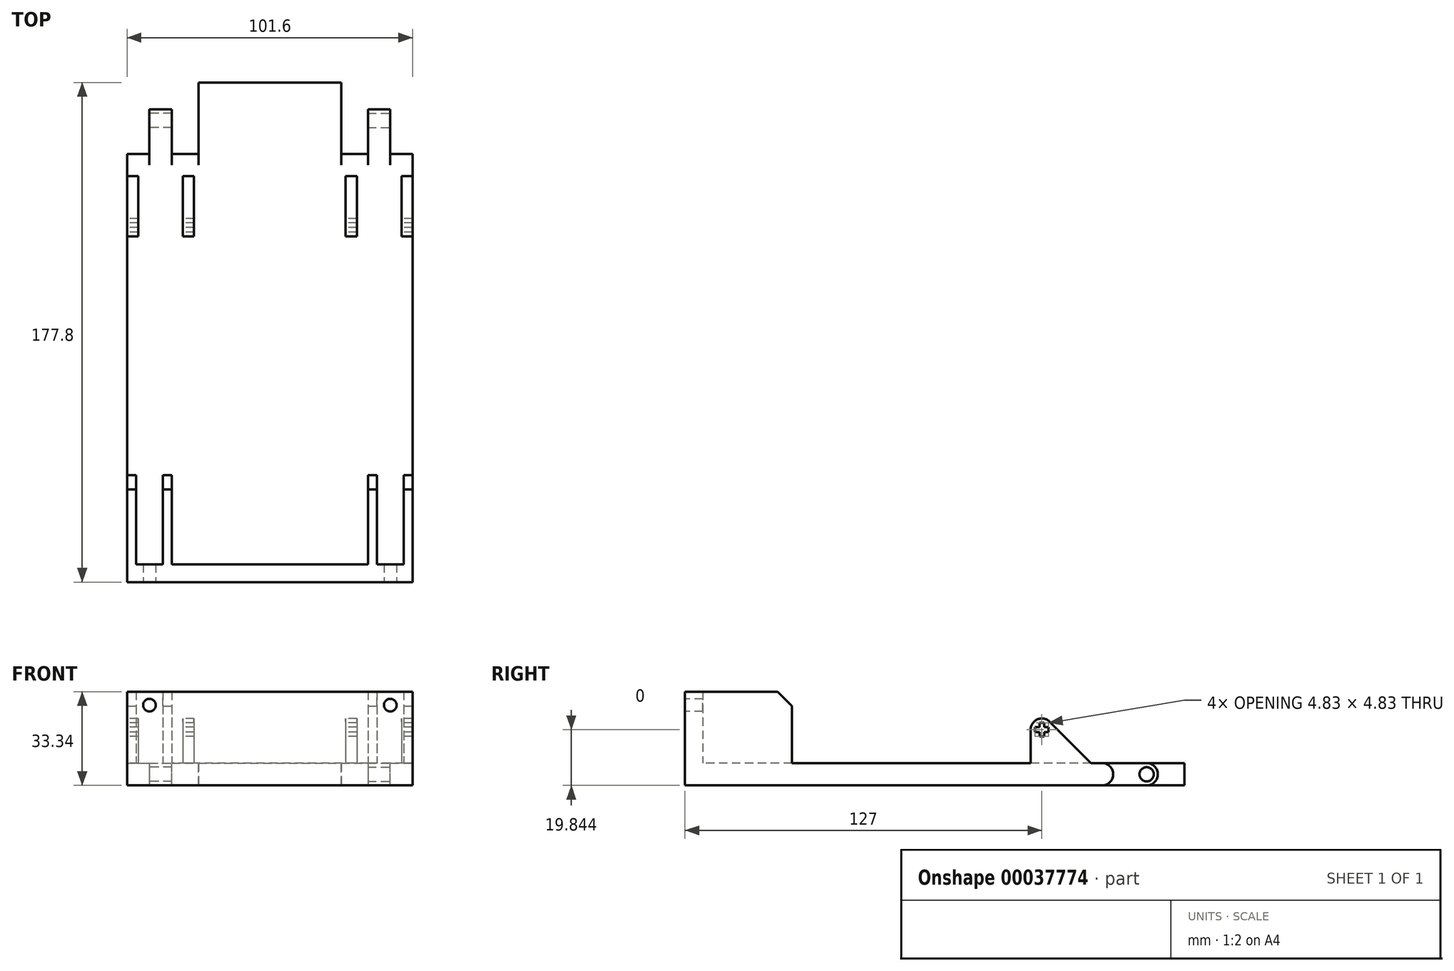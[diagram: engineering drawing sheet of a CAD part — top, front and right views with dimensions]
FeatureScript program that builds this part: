
annotation { "Feature Type Name" : "Feature", "Feature Type Description" : "" }
export const myFeature = defineFeature(function(context is Context, id is Id, definition is map)
    precondition{}
    {
        {
            var Q0;
            Q0=qCreatedBy(makeId("Top.planeOp"),FACE);
            var sketch = newSketch(context, id + "F0", { "sketchPlane" : qUnion([Q0])});
            skLineSegment(sketch, "E0.bottom", {"start": v(0, 0) * mm, "end": v(101.6, 0) * mm});
            skLineSegment(sketch, "E0.left", {"start": v(0, 0) * mm, "end": v(0, 152.4) * mm});
            skLineSegment(sketch, "E1.right", {"start": v(25.4, 177.8) * mm, "end": v(25.4, 152.4) * mm});
            skLineSegment(sketch, "E2", {"start": v(0, 152.4) * mm, "end": v(7.94, 152.4) * mm});
            skLineSegment(sketch, "E3", {"start": v(7.94, 152.4) * mm, "end": v(7.94, 168.28) * mm});
            skLineSegment(sketch, "E4", {"start": v(7.94, 168.28) * mm, "end": v(15.88, 168.28) * mm});
            skLineSegment(sketch, "E5", {"start": v(15.88, 168.28) * mm, "end": v(15.88, 152.4) * mm});
            skLineSegment(sketch, "E6", {"start": v(15.88, 152.4) * mm, "end": v(25.4, 152.4) * mm});
            skLineSegment(sketch, "E7", {"start": v(7.94, 152.4) * mm, "end": v(15.88, 152.4) * mm, "construction": true});
            skLineSegment(sketch, "E8", {"start": v(25.4, 177.8) * mm, "end": v(76.2, 177.8) * mm});
            skLineSegment(sketch, "E9", {"start": v(76.2, 177.8) * mm, "end": v(76.2, 152.4) * mm});
            skLineSegment(sketch, "E10", {"start": v(76.2, 152.4) * mm, "end": v(85.72, 152.4) * mm});
            skLineSegment(sketch, "E11", {"start": v(85.72, 152.4) * mm, "end": v(85.72, 168.28) * mm});
            skLineSegment(sketch, "E12", {"start": v(85.72, 168.28) * mm, "end": v(93.66, 168.28) * mm});
            skLineSegment(sketch, "E13", {"start": v(93.66, 168.28) * mm, "end": v(93.66, 152.4) * mm});
            skLineSegment(sketch, "E14", {"start": v(93.66, 152.4) * mm, "end": v(101.6, 152.4) * mm});
            skLineSegment(sketch, "E15", {"start": v(101.6, 152.4) * mm, "end": v(101.6, 0) * mm});
            skSolve(sketch);
        }
        {
            var Q0;
            Q0=qSketchRegion(id+"F0",true);
            extrude(context, id + "F1", {"entities" : qUnion([Q0]), "depth" : 7.94 * mm});
        }
        {
            var Q0;
            Q0=makeQuery(id+"F1.opExtrude","CAP_EDGE",EDGE,{"disambiguationData":[OSD([sQuery(id+"F0.wireOp",EDGE,"E6")])],"isStart":true});
            var Q1;
            Q1=makeQuery(id+"F1.opExtrude","CAP_EDGE",EDGE,{"disambiguationData":[OSD([sQuery(id+"F0.wireOp",EDGE,"E6")])],"isStart":false});
            var Q2;
            Q2=makeQuery(id+"F1.opExtrude","CAP_EDGE",EDGE,{"disambiguationData":[OSD([sQuery(id+"F0.wireOp",EDGE,"E4")])],"isStart":true});
            var Q3;
            Q3=makeQuery(id+"F1.opExtrude","CAP_EDGE",EDGE,{"disambiguationData":[OSD([sQuery(id+"F0.wireOp",EDGE,"E4")])],"isStart":false});
            var Q4;
            Q4=makeQuery(id+"F1.opExtrude","CAP_EDGE",EDGE,{"disambiguationData":[OSD([sQuery(id+"F0.wireOp",EDGE,"E2")])],"isStart":true});
            var Q5;
            Q5=makeQuery(id+"F1.opExtrude","CAP_EDGE",EDGE,{"disambiguationData":[OSD([sQuery(id+"F0.wireOp",EDGE,"E2")])],"isStart":false});
            var Q6;
            Q6=makeQuery(id+"F1.opExtrude","CAP_EDGE",EDGE,{"disambiguationData":[OSD([sQuery(id+"F0.wireOp",EDGE,"E10")])],"isStart":false});
            var Q7;
            Q7=makeQuery(id+"F1.opExtrude","CAP_EDGE",EDGE,{"disambiguationData":[OSD([sQuery(id+"F0.wireOp",EDGE,"E10")])],"isStart":true});
            var Q8;
            Q8=makeQuery(id+"F1.opExtrude","CAP_EDGE",EDGE,{"disambiguationData":[OSD([sQuery(id+"F0.wireOp",EDGE,"E14")])],"isStart":true});
            var Q9;
            Q9=makeQuery(id+"F1.opExtrude","CAP_EDGE",EDGE,{"disambiguationData":[OSD([sQuery(id+"F0.wireOp",EDGE,"E14")])],"isStart":false});
            var Q10;
            Q10=makeQuery(id+"F1.opExtrude","CAP_EDGE",EDGE,{"disambiguationData":[OSD([sQuery(id+"F0.wireOp",EDGE,"E12")])],"isStart":false});
            var Q11;
            Q11=makeQuery(id+"F1.opExtrude","CAP_EDGE",EDGE,{"disambiguationData":[OSD([sQuery(id+"F0.wireOp",EDGE,"E12")])],"isStart":true});
            fillet(context, id + "F2", {"entities" : qUnion([Q0, Q1, Q2, Q3, Q4, Q5, Q6, Q7, Q8, Q9, Q10, Q11]), "radius" : 3.97 * mm, "tangentPropagation" : true, "allowEdgeOverflow" : false});
        }
        {
            var Q0;
            Q0=makeQuery(id+"FNYOd53glhffsHS_1.boolean.opBoolean","MERGE",FACE,{"derivedFrom":[makeQuery(id+"F1.opExtrude","SWEPT_FACE",FACE,{"disambiguationData":[OSD([sQuery(id+"F0.wireOp",EDGE,"E0.left")])]}),makeQuery(id+"FNYOd53glhffsHS_1.opExtrude","SWEPT_FACE",FACE,{"disambiguationData":[OSD([sQuery(id+"F2h7VdxgF09O83Z_1.wireOp",EDGE,"9d81e400-ffae-42b2-a3b4-f3f00290e241.left")])]})]});
            var sketch = newSketch(context, id + "F3", { "sketchPlane" : qUnion([Q0])});
            skCircle(sketch, "E16", {"center": v(-164.3, 3.97) * mm, "radius": 2.54 * mm});
            skSolve(sketch);
        }
        {
            var Q0;
            Q0=qSketchRegion(id+"F3",true);
            var Q1;
            Q1=makeQuery(id+"FNYOd53glhffsHS_1.boolean.opBoolean","MERGE",FACE,{"derivedFrom":[makeQuery(id+"F1.opExtrude","SWEPT_FACE",FACE,{"disambiguationData":[OSD([sQuery(id+"F0.wireOp",EDGE,"E1.right")])]}),makeQuery(id+"FNYOd53glhffsHS_1.opExtrude","SWEPT_FACE",FACE,{"disambiguationData":[OSD([sQuery(id+"F2h7VdxgF09O83Z_1.wireOp",EDGE,"894c2ef8-1dbc-4df3-bad7-f21cdf97773c.left")])]})]});
            extrude(context, id + "F4", {"entities" : qUnion([Q0]), "operationType" : NewBodyOperationType.REMOVE, "endBound" : BoundingType.UP_TO_SURFACE, "oppositeDirection" : true, "endBoundEntityFace" : qUnion([Q1]), "depth" : 25.4 * mm});
        }
        {
            var Q0;
            Q0=makeQuery(id+"F1.opExtrude","SWEPT_FACE",FACE,{"disambiguationData":[OSD([sQuery(id+"F0.wireOp",EDGE,"E13")])]});
            var sketch = newSketch(context, id + "F5", { "sketchPlane" : qUnion([Q0])});
            skCircle(sketch, "E17", {"center": v(164.3, 3.97) * mm, "radius": 2.54 * mm});
            skSolve(sketch);
        }
        {
            var Q0;
            Q0 = qSketchRegion(id + "F5", true);
            var Q1;
            Q1=makeQuery(id+"F1.opExtrude","SWEPT_FACE",FACE,{"disambiguationData":[OSD([sQuery(id+"F0.wireOp",EDGE,"E11")])]});
            extrude(context, id + "F6", {"entities" : qUnion([Q0]), "operationType" : NewBodyOperationType.REMOVE, "endBound" : BoundingType.UP_TO_SURFACE, "oppositeDirection" : true, "endBoundEntityFace" : qUnion([Q1]), "depth" : 25.4 * mm});
        }
        {
            var Q0;
            Q0=makeQuery(id+"F1.opExtrude","CAP_FACE",FACE,{"disambiguationData":[OSD([sQuery(id+"F0.wireOp",EDGE,"E0.bottom"),sQuery(id+"F0.wireOp",EDGE,"E0.left"),sQuery(id+"F0.wireOp",EDGE,"E1.right"),sQuery(id+"F0.wireOp",EDGE,"E2"),sQuery(id+"F0.wireOp",EDGE,"E3"),sQuery(id+"F0.wireOp",EDGE,"E4"),sQuery(id+"F0.wireOp",EDGE,"E5"),sQuery(id+"F0.wireOp",EDGE,"E6"),sQuery(id+"F0.wireOp",EDGE,"E8"),sQuery(id+"F0.wireOp",EDGE,"E9"),sQuery(id+"F0.wireOp",EDGE,"E10"),sQuery(id+"F0.wireOp",EDGE,"E11"),sQuery(id+"F0.wireOp",EDGE,"E12"),sQuery(id+"F0.wireOp",EDGE,"E13"),sQuery(id+"F0.wireOp",EDGE,"E14"),sQuery(id+"F0.wireOp",EDGE,"E15")])],"isStart":false});
            var sketch = newSketch(context, id + "F7", { "sketchPlane" : qUnion([Q0])});
            skLineSegment(sketch, "E18.bottom", {"start": v(0, 148.43) * mm, "end": v(3.97, 148.43) * mm});
            skLineSegment(sketch, "E18.top", {"start": v(0, 123.03) * mm, "end": v(3.97, 123.03) * mm});
            skLineSegment(sketch, "E18.left", {"start": v(0, 148.43) * mm, "end": v(0, 123.03) * mm});
            skLineSegment(sketch, "E18.right", {"start": v(3.97, 148.43) * mm, "end": v(3.97, 123.03) * mm});
            skLineSegment(sketch, "E19.bottom", {"start": v(23.81, 148.43) * mm, "end": v(19.84, 148.43) * mm});
            skLineSegment(sketch, "E19.top", {"start": v(23.81, 123.03) * mm, "end": v(19.84, 123.03) * mm});
            skLineSegment(sketch, "E19.left", {"start": v(23.81, 148.43) * mm, "end": v(23.81, 123.03) * mm});
            skLineSegment(sketch, "E19.right", {"start": v(19.84, 148.43) * mm, "end": v(19.84, 123.03) * mm});
            skLineSegment(sketch, "E20.bottom", {"start": v(101.6, 148.43) * mm, "end": v(97.63, 148.43) * mm});
            skLineSegment(sketch, "E20.top", {"start": v(101.6, 123.03) * mm, "end": v(97.63, 123.03) * mm});
            skLineSegment(sketch, "E20.left", {"start": v(101.6, 148.43) * mm, "end": v(101.6, 123.03) * mm});
            skLineSegment(sketch, "E20.right", {"start": v(97.63, 148.43) * mm, "end": v(97.63, 123.03) * mm});
            skLineSegment(sketch, "E21.bottom", {"start": v(77.79, 148.43) * mm, "end": v(81.76, 148.43) * mm});
            skLineSegment(sketch, "E21.top", {"start": v(77.79, 123.03) * mm, "end": v(81.76, 123.03) * mm});
            skLineSegment(sketch, "E21.left", {"start": v(77.79, 148.43) * mm, "end": v(77.79, 123.03) * mm});
            skLineSegment(sketch, "E21.right", {"start": v(81.76, 148.43) * mm, "end": v(81.76, 123.03) * mm});
            skLineSegment(sketch, "E22", {"start": v(3.97, 123.03) * mm, "end": v(19.84, 123.03) * mm, "construction": true});
            skLineSegment(sketch, "E23", {"start": v(81.76, 123.03) * mm, "end": v(97.63, 123.03) * mm, "construction": true});
            skSolve(sketch);
        }
        {
            var Q0;
            Q0 = qSketchRegion(id + "F7", true);
            extrude(context, id + "F8", {"entities" : qUnion([Q0]), "operationType" : NewBodyOperationType.ADD, "depth" : 15.88 * mm});
        }
        {
            var Q0;
            Q0=makeQuery(id+"F8.boolean.opBoolean","MERGE",FACE,{"derivedFrom":[makeQuery(id+"F1.opExtrude","SWEPT_FACE",FACE,{"disambiguationData":[OSD([sQuery(id+"F0.wireOp",EDGE,"E0.left")])]}),makeQuery(id+"F8.opExtrude","SWEPT_FACE",FACE,{"disambiguationData":[OSD([sQuery(id+"F7.wireOp",EDGE,"E18.left")])]})]});
            var sketch = newSketch(context, id + "F9", { "sketchPlane" : qUnion([Q0])});
            skLineSegment(sketch, "E24.bottom", {"start": v(-123.03, 23.81) * mm, "end": v(-148.43, 23.81) * mm});
            skLineSegment(sketch, "E24.top", {"start": v(-123.03, 7.94) * mm, "end": v(-148.43, 7.94) * mm});
            skLineSegment(sketch, "E24.left", {"start": v(-123.03, 23.81) * mm, "end": v(-123.03, 7.94) * mm});
            skLineSegment(sketch, "E24.right", {"start": v(-148.43, 23.81) * mm, "end": v(-148.43, 7.94) * mm});
            skLineSegment(sketch, "E25", {"start": v(-144.52, 7.94) * mm, "end": v(-129.8, 22.65) * mm});
            skArc(sketch, "E26", {"start": v(-123.03, 19.84) * mm, "mid": v(-125.48, 23.51) * mm, "end": v(-129.8, 22.65) * mm});
            skLineSegment(sketch, "E27.rect.bottom", {"start": v(-126.16, 17.43) * mm, "end": v(-127.84, 17.43) * mm});
            skLineSegment(sketch, "E27.rect.top", {"start": v(-126.16, 22.26) * mm, "end": v(-127.84, 22.26) * mm});
            skLineSegment(sketch, "E27.rect.left", {"start": v(-126.16, 17.43) * mm, "end": v(-126.16, 22.26) * mm});
            skLineSegment(sketch, "E27.rect.right", {"start": v(-127.84, 17.43) * mm, "end": v(-127.84, 22.26) * mm});
            skLineSegment(sketch, "E28.rect.bottom", {"start": v(-124.59, 19) * mm, "end": v(-129.41, 19) * mm});
            skLineSegment(sketch, "E28.rect.top", {"start": v(-124.59, 20.69) * mm, "end": v(-129.41, 20.69) * mm});
            skLineSegment(sketch, "E28.rect.left", {"start": v(-124.59, 19) * mm, "end": v(-124.59, 20.69) * mm});
            skLineSegment(sketch, "E28.rect.right", {"start": v(-129.41, 19) * mm, "end": v(-129.41, 20.69) * mm});
            skSolve(sketch);
        }
        {
            var Q0;
            {var subQ0=sQuery(id+"F9.wireOp",EDGE,"E24.left");var subQ3=sQuery(id+"F9.wireOp",EDGE,"E24.bottom");var subQ4=makeQuery(id+"F9.imprint","INTERSECT",VERTEX,{"derivedFrom":[subQ3,subQ0]});Q0=makeQuery(id+"F9.imprint","IMPRINT",FACE,{"disambiguationData":[TD([[makeQuery(id+"F9.imprint","IMPRINT",EDGE,{"disambiguationData":[TD([[subQ4,-1.0]])],"derivedFrom":subQ3}),1.0]])]});}
            var Q1;
            {var subQ4=sQuery(id+"F9.wireOp",EDGE,"E24.right");Q1=makeQuery(id+"F9.imprint","IMPRINT",FACE,{"disambiguationData":[TD([[makeQuery(id+"F9.imprint","IMPRINT",EDGE,{"derivedFrom":subQ4}),1.0]])]});}
            var Q2;
            {var subQ5=sQuery(id+"F9.wireOp",EDGE,"E27.rect.bottom");Q2=makeQuery(id+"F9.imprint","IMPRINT",FACE,{"disambiguationData":[TD([[makeQuery(id+"F9.imprint","IMPRINT",EDGE,{"derivedFrom":subQ5}),-1.0]])]});}
            var Q3;
            {var subQ3=sQuery(id+"F9.wireOp",EDGE,"E27.rect.left");var subQ5=sQuery(id+"F9.wireOp",EDGE,"E28.rect.bottom");var subQ7=makeQuery(id+"F9.imprint","INTERSECT",VERTEX,{"derivedFrom":[subQ3,subQ5]});Q3=makeQuery(id+"F9.imprint","IMPRINT",FACE,{"disambiguationData":[TD([[makeQuery(id+"F9.imprint","IMPRINT",EDGE,{"disambiguationData":[TD([[subQ7,-1.0]])],"derivedFrom":subQ3}),1.0]])]});}
            var Q4;
            {var subQ3=sQuery(id+"F9.wireOp",EDGE,"E28.rect.left");Q4=makeQuery(id+"F9.imprint","IMPRINT",FACE,{"disambiguationData":[TD([[makeQuery(id+"F9.imprint","IMPRINT",EDGE,{"derivedFrom":subQ3}),1.0]])]});}
            var Q5;
            {var subQ5=sQuery(id+"F9.wireOp",EDGE,"E27.rect.top");Q5=makeQuery(id+"F9.imprint","IMPRINT",FACE,{"disambiguationData":[TD([[makeQuery(id+"F9.imprint","IMPRINT",EDGE,{"derivedFrom":subQ5}),1.0]])]});}
            var Q6;
            {var subQ0=sQuery(id+"F9.wireOp",EDGE,"E28.rect.right");Q6=makeQuery(id+"F9.imprint","IMPRINT",FACE,{"disambiguationData":[TD([[makeQuery(id+"F9.imprint","IMPRINT",EDGE,{"derivedFrom":subQ0}),-1.0]])]});}
            var Q7;
            Q7=makeQuery(id+"F8.boolean.opBoolean","MERGE",FACE,{"derivedFrom":[makeQuery(id+"F1.opExtrude","SWEPT_FACE",FACE,{"disambiguationData":[OSD([sQuery(id+"F0.wireOp",EDGE,"E15")])]}),makeQuery(id+"F8.opExtrude","SWEPT_FACE",FACE,{"disambiguationData":[OSD([sQuery(id+"F7.wireOp",EDGE,"E20.left")])]})]});
            extrude(context, id + "F10", {"entities" : qUnion([Q0, Q1, Q2, Q3, Q4, Q5, Q6]), "operationType" : NewBodyOperationType.REMOVE, "endBound" : BoundingType.UP_TO_SURFACE, "oppositeDirection" : true, "endBoundEntityFace" : qUnion([Q7]), "depth" : 25.4 * mm});
        }
        {
            var Q0;
            Q0=makeQuery(id+"F10.boolean.opBoolean","MERGE",FACE,{"derivedFrom":[makeQuery(id+"F1.opExtrude","CAP_FACE",FACE,{"disambiguationData":[OSD([sQuery(id+"F0.wireOp",EDGE,"E0.bottom"),sQuery(id+"F0.wireOp",EDGE,"E0.left"),sQuery(id+"F0.wireOp",EDGE,"E1.right"),sQuery(id+"F0.wireOp",EDGE,"E2"),sQuery(id+"F0.wireOp",EDGE,"E3"),sQuery(id+"F0.wireOp",EDGE,"E4"),sQuery(id+"F0.wireOp",EDGE,"E5"),sQuery(id+"F0.wireOp",EDGE,"E6"),sQuery(id+"F0.wireOp",EDGE,"E8"),sQuery(id+"F0.wireOp",EDGE,"E9"),sQuery(id+"F0.wireOp",EDGE,"E10"),sQuery(id+"F0.wireOp",EDGE,"E11"),sQuery(id+"F0.wireOp",EDGE,"E12"),sQuery(id+"F0.wireOp",EDGE,"E13"),sQuery(id+"F0.wireOp",EDGE,"E14"),sQuery(id+"F0.wireOp",EDGE,"E15")])],"isStart":false}),makeQuery(id+"F10.opExtrude","SWEPT_FACE",FACE,{"disambiguationData":[OSD([sQuery(id+"F9.wireOp",EDGE,"E24.top")])]})]});
            var sketch = newSketch(context, id + "F11", { "sketchPlane" : qUnion([Q0])});
            skLineSegment(sketch, "E29.bottom", {"start": v(0, 0) * mm, "end": v(101.6, 0) * mm});
            skLineSegment(sketch, "E29.left", {"start": v(0, 0) * mm, "end": v(0, 38.1) * mm});
            skLineSegment(sketch, "E29.right", {"start": v(101.6, 0) * mm, "end": v(101.6, 38.1) * mm});
            skLineSegment(sketch, "E30", {"start": v(0, 38.1) * mm, "end": v(3.18, 38.1) * mm});
            skLineSegment(sketch, "E31", {"start": v(3.18, 38.1) * mm, "end": v(3.18, 6.35) * mm});
            skLineSegment(sketch, "E32", {"start": v(3.18, 6.35) * mm, "end": v(12.7, 6.35) * mm});
            skLineSegment(sketch, "E33", {"start": v(12.7, 6.35) * mm, "end": v(12.7, 38.1) * mm});
            skLineSegment(sketch, "E34", {"start": v(12.7, 38.1) * mm, "end": v(15.88, 38.1) * mm});
            skLineSegment(sketch, "E35", {"start": v(15.88, 38.1) * mm, "end": v(15.88, 6.35) * mm});
            skLineSegment(sketch, "E36", {"start": v(101.6, 38.1) * mm, "end": v(98.42, 38.1) * mm});
            skLineSegment(sketch, "E37", {"start": v(98.42, 38.1) * mm, "end": v(98.42, 6.35) * mm});
            skLineSegment(sketch, "E38", {"start": v(98.42, 6.35) * mm, "end": v(88.9, 6.35) * mm});
            skLineSegment(sketch, "E39", {"start": v(88.9, 6.35) * mm, "end": v(88.9, 38.1) * mm});
            skLineSegment(sketch, "E40", {"start": v(88.9, 38.1) * mm, "end": v(85.72, 38.1) * mm});
            skLineSegment(sketch, "E41", {"start": v(85.72, 38.1) * mm, "end": v(85.72, 6.35) * mm});
            skLineSegment(sketch, "E42", {"start": v(85.72, 6.35) * mm, "end": v(15.87, 6.35) * mm});
            skLineSegment(sketch, "E43", {"start": v(50.8, 6.35) * mm, "end": v(50.8, 0) * mm, "construction": true});
            skSolve(sketch);
        }
        {
            var Q0;
            Q0 = qSketchRegion(id + "F11", true);
            extrude(context, id + "F12", {"entities" : qUnion([Q0]), "operationType" : NewBodyOperationType.ADD, "depth" : 25.4 * mm});
        }
        {
            var Q0;
            Q0=makeQuery(id+"F12.opExtrude","CAP_EDGE",EDGE,{"disambiguationData":[OSD([sQuery(id+"F11.wireOp",EDGE,"E34")])],"isStart":false});
            var Q1;
            Q1=makeQuery(id+"F12.opExtrude","CAP_EDGE",EDGE,{"disambiguationData":[OSD([sQuery(id+"F11.wireOp",EDGE,"E30")])],"isStart":false});
            var Q2;
            Q2=makeQuery(id+"F12.opExtrude","CAP_EDGE",EDGE,{"disambiguationData":[OSD([sQuery(id+"F11.wireOp",EDGE,"E40")])],"isStart":false});
            var Q3;
            Q3=makeQuery(id+"F12.opExtrude","CAP_EDGE",EDGE,{"disambiguationData":[OSD([sQuery(id+"F11.wireOp",EDGE,"E36")])],"isStart":false});
            chamfer(context, id + "F13", {"entities" : qUnion([Q0, Q1, Q2, Q3]), "width" : 5.08 * mm, "tangentPropagation" : true});
        }
        {
            var Q0;
            Q0=makeQuery(id+"F12.boolean.opBoolean","MERGE",FACE,{"derivedFrom":[makeQuery(id+"F1.opExtrude","SWEPT_FACE",FACE,{"disambiguationData":[OSD([sQuery(id+"F0.wireOp",EDGE,"E0.bottom")])]}),makeQuery(id+"F12.opExtrude","SWEPT_FACE",FACE,{"disambiguationData":[OSD([sQuery(id+"F11.wireOp",EDGE,"E29.bottom")])]})]});
            var sketch = newSketch(context, id + "F14", { "sketchPlane" : qUnion([Q0])});
            skLineSegment(sketch, "E44", {"start": v(7.94, 33.34) * mm, "end": v(7.94, 28.58) * mm, "construction": true});
            skLineSegment(sketch, "E45", {"start": v(93.66, 33.34) * mm, "end": v(93.66, 28.58) * mm, "construction": true});
            skCircle(sketch, "E46", {"center": v(93.66, 28.58) * mm, "radius": 2.25 * mm});
            skCircle(sketch, "E47", {"center": v(7.94, 28.58) * mm, "radius": 2.25 * mm});
            skSolve(sketch);
        }
        {
            var Q0;
            Q0 = qSketchRegion(id + "F14", true);
            var Q1;
            Q1=makeQuery(id+"F12.opExtrude","SWEPT_FACE",FACE,{"disambiguationData":[OSD([sQuery(id+"F11.wireOp",EDGE,"E42")])]});
            extrude(context, id + "F15", {"entities" : qUnion([Q0]), "operationType" : NewBodyOperationType.REMOVE, "endBound" : BoundingType.UP_TO_SURFACE, "oppositeDirection" : true, "endBoundEntityFace" : qUnion([Q1]), "depth" : 25.4 * mm});
        }
    });
